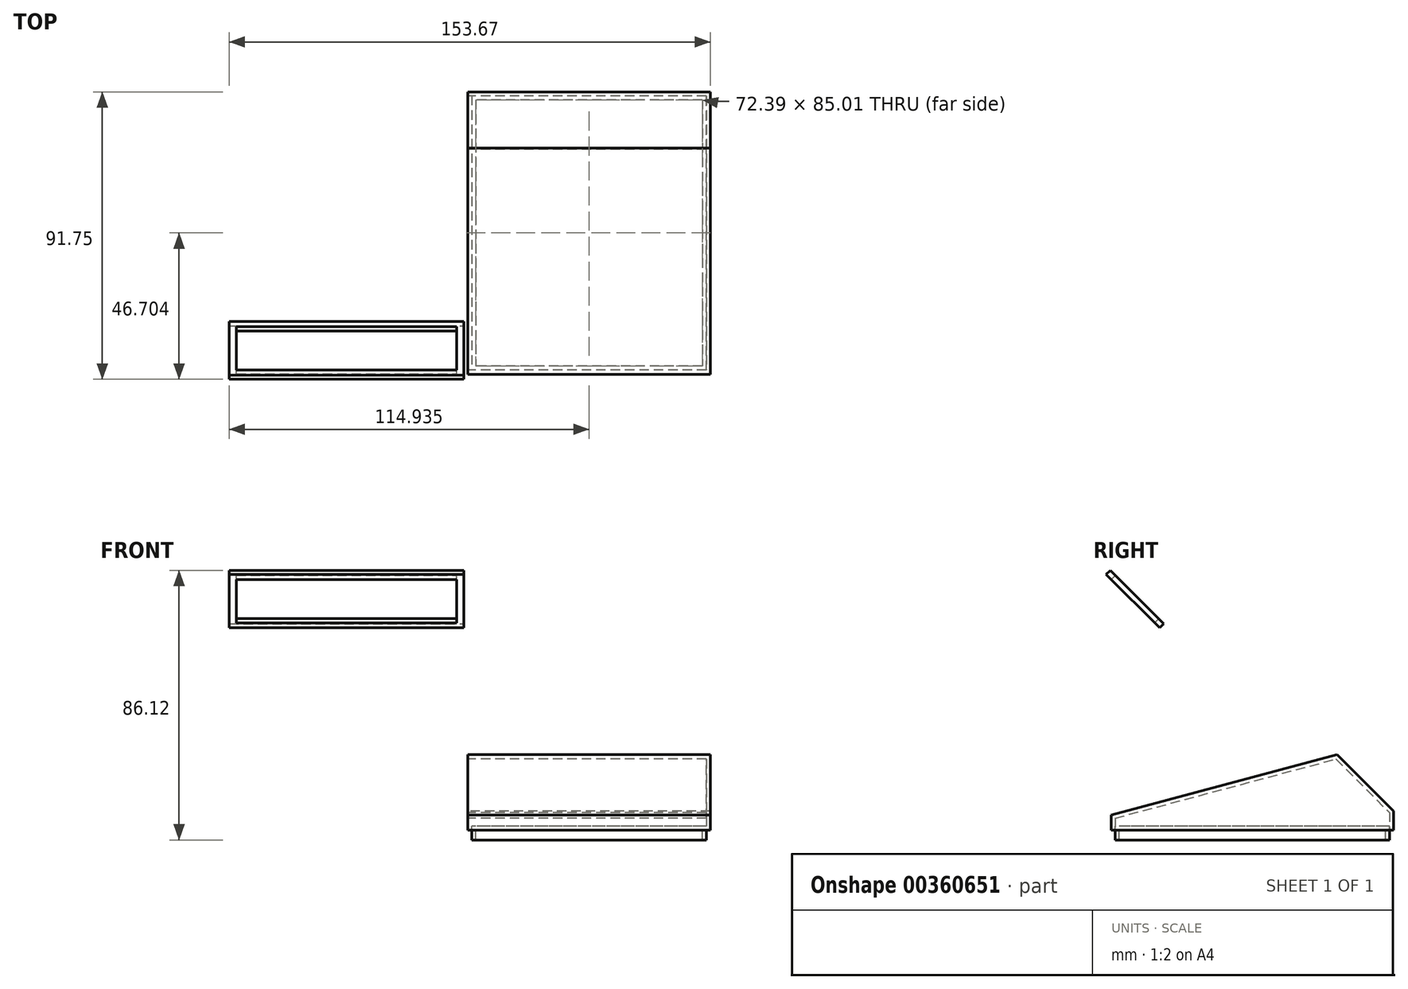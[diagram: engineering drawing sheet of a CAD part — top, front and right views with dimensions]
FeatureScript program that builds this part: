
annotation { "Feature Type Name" : "Feature", "Feature Type Description" : "" }
export const myFeature = defineFeature(function(context is Context, id is Id, definition is map)
    precondition{}
    {
        {
            var Q0;
            Q0=qCreatedBy(makeId("Right.planeOp"),FACE);
            var sketch = newSketch(context, id + "F0", { "sketchPlane" : qUnion([Q0])});
            skLineSegment(sketch, "E0", {"start": v(90.17, 0) * mm, "end": v(88.9, 0) * mm});
            skLineSegment(sketch, "E1", {"start": v(0, 4.76) * mm, "end": v(72.2, 24.05) * mm});
            skLineSegment(sketch, "E2", {"start": v(72.2, 24.05) * mm, "end": v(90.17, 6.1) * mm});
            skLineSegment(sketch, "E3", {"start": v(90.17, 6.1) * mm, "end": v(90.17, 0) * mm});
            skLineSegment(sketch, "E4.0", {"start": v(88.9, 5.57) * mm, "end": v(88.9, 0) * mm});
            skLineSegment(sketch, "E4.1", {"start": v(71.83, 22.64) * mm, "end": v(88.9, 5.57) * mm});
            skLineSegment(sketch, "E4.2", {"start": v(1.35, 3.8) * mm, "end": v(71.83, 22.64) * mm});
            skLineSegment(sketch, "E5", {"start": v(0, 4.76) * mm, "end": v(0, 0) * mm});
            skLineSegment(sketch, "E6", {"start": v(1.35, 3.8) * mm, "end": v(1.35, 0) * mm});
            skLineSegment(sketch, "E7.trimOffspring", {"start": v(1.35, 0) * mm, "end": v(0, 0) * mm});
            skLineSegment(sketch, "E8", {"start": v(88.9, 0) * mm, "end": v(90.17, 0) * mm});
            skLineSegment(sketch, "E9", {"start": v(0, 0) * mm, "end": v(1.35, 0) * mm});
            skSolve(sketch);
        }
        {
            var Q0;
            Q0 = qSketchRegion(id + "F0", true);
            extrude(context, id + "F1", {"entities" : qUnion([Q0]), "depth" : 77.47 * mm, "offsetDistance" : 25.4 * mm});
        }
        {
            var Q0;
            Q0=makeQuery(id+"F1.opExtrude","CAP_FACE",FACE,{"disambiguationData":[OSD([sQuery(id+"F0.wireOp",EDGE,"E1"),sQuery(id+"F0.wireOp",EDGE,"E2"),sQuery(id+"F0.wireOp",EDGE,"E3"),sQuery(id+"F0.wireOp",EDGE,"E4.0"),sQuery(id+"F0.wireOp",EDGE,"E4.1"),sQuery(id+"F0.wireOp",EDGE,"E4.2"),sQuery(id+"F0.wireOp",EDGE,"E5"),sQuery(id+"F0.wireOp",EDGE,"E6"),sQuery(id+"F0.wireOp",EDGE,"E8"),sQuery(id+"F0.wireOp",EDGE,"E9")])],"isStart":false});
            var sketch = newSketch(context, id + "F2", { "sketchPlane" : qUnion([Q0])});
            skLineSegment(sketch, "E10", {"start": v(90.17, 0) * mm, "end": v(0, 0) * mm});
            skLineSegment(sketch, "E11.0", {"start": v(0, 4.76) * mm, "end": v(72.2, 24.05) * mm});
            skLineSegment(sketch, "E11.1", {"start": v(0, 4.76) * mm, "end": v(0, 0) * mm});
            skLineSegment(sketch, "E11.2", {"start": v(72.2, 24.05) * mm, "end": v(90.17, 6.1) * mm});
            skLineSegment(sketch, "E11.3", {"start": v(90.17, 6.1) * mm, "end": v(90.17, 0) * mm});
            skSolve(sketch);
        }
        {
            var Q0;
            Q0 = qSketchRegion(id + "F2", true);
            extrude(context, id + "F3", {"entities" : qUnion([Q0]), "operationType" : NewBodyOperationType.ADD, "oppositeDirection" : true, "depth" : 1.27 * mm, "offsetDistance" : 25.4 * mm});
        }
        {
            var Q0;
            Q0=makeQuery(id+"F3.boolean.opBoolean","MERGE",FACE,{"derivedFrom":[makeQuery(id+"F1.opExtrude","CAP_FACE",FACE,{"disambiguationData":[OSD([sQuery(id+"F0.wireOp",EDGE,"E1"),sQuery(id+"F0.wireOp",EDGE,"E2"),sQuery(id+"F0.wireOp",EDGE,"E3"),sQuery(id+"F0.wireOp",EDGE,"E4.0"),sQuery(id+"F0.wireOp",EDGE,"E4.1"),sQuery(id+"F0.wireOp",EDGE,"E4.2"),sQuery(id+"F0.wireOp",EDGE,"E5"),sQuery(id+"F0.wireOp",EDGE,"E6"),sQuery(id+"F0.wireOp",EDGE,"E8"),sQuery(id+"F0.wireOp",EDGE,"E9")])],"isStart":false}),makeQuery(id+"F3.opExtrude","CAP_FACE",FACE,{"disambiguationData":[OSD([sQuery(id+"F2.wireOp",EDGE,"E10"),sQuery(id+"F2.wireOp",EDGE,"E11.0"),sQuery(id+"F2.wireOp",EDGE,"E11.1"),sQuery(id+"F2.wireOp",EDGE,"E11.2"),sQuery(id+"F2.wireOp",EDGE,"E11.3")])],"isStart":true})]});
            var Q1;
            Q1=makeQuery(id+"F1.opExtrude","CAP_FACE",FACE,{"disambiguationData":[OSD([sQuery(id+"F0.wireOp",EDGE,"E1"),sQuery(id+"F0.wireOp",EDGE,"E2"),sQuery(id+"F0.wireOp",EDGE,"E3"),sQuery(id+"F0.wireOp",EDGE,"E4.0"),sQuery(id+"F0.wireOp",EDGE,"E4.1"),sQuery(id+"F0.wireOp",EDGE,"E4.2"),sQuery(id+"F0.wireOp",EDGE,"E5"),sQuery(id+"F0.wireOp",EDGE,"E6"),sQuery(id+"F0.wireOp",EDGE,"E8"),sQuery(id+"F0.wireOp",EDGE,"E9")])],"isStart":true});
            cPlane(context, id + "F4", {"entities" : qUnion([Q0, Q1]), "cplaneType" : CPlaneType.MID_PLANE, "offset" : 25.4 * mm, "width" : 152.4 * mm, "height" : 152.4 * mm});
        }
        {
            var Q0;
            {var subQ0=sQuery(id+"F2.wireOp",EDGE,"E10");Q0=makeQuery(id+"FamEGNvEXDgyTqM_1.1.F3.boolean.opBoolean","MERGE",FACE,{"derivedFrom":[makeQuery(id+"F3.boolean.opBoolean","MERGE",FACE,{"derivedFrom":[makeQuery(id+"F1.opExtrude","SWEPT_FACE",FACE,{"disambiguationData":[OSD([sQuery(id+"F0.wireOp",EDGE,"E8")])]}),makeQuery(id+"F1.opExtrude","SWEPT_FACE",FACE,{"disambiguationData":[OSD([sQuery(id+"F0.wireOp",EDGE,"E9")])]}),makeQuery(id+"F3.opExtrude","SWEPT_FACE",FACE,{"disambiguationData":[OSD([subQ0])]})]}),makeQuery(id+"FamEGNvEXDgyTqM_1.1.F3.opExtrude","SWEPT_FACE",FACE,{"disambiguationData":[OSD([subQ0])]})]});}
            var sketch = newSketch(context, id + "F5", { "sketchPlane" : qUnion([Q0])});
            skLineSegment(sketch, "E12.0", {"start": v(76.2, -1.35) * mm, "end": v(1.27, -1.35) * mm});
            skLineSegment(sketch, "E12.1", {"start": v(1.27, -88.9) * mm, "end": v(1.27, -1.35) * mm});
            skLineSegment(sketch, "E12.2", {"start": v(76.2, -88.9) * mm, "end": v(76.2, -1.35) * mm});
            skLineSegment(sketch, "E12.3", {"start": v(76.2, -88.9) * mm, "end": v(1.27, -88.9) * mm});
            skLineSegment(sketch, "E13.0", {"start": v(74.93, -2.62) * mm, "end": v(2.54, -2.62) * mm});
            skLineSegment(sketch, "E13.1", {"start": v(74.93, -87.63) * mm, "end": v(74.93, -2.62) * mm});
            skLineSegment(sketch, "E13.2", {"start": v(74.93, -87.63) * mm, "end": v(2.54, -87.63) * mm});
            skLineSegment(sketch, "E13.3", {"start": v(2.54, -87.63) * mm, "end": v(2.54, -2.62) * mm});
            skSolve(sketch);
        }
        {
            var Q0;
            Q0 = qSketchRegion(id + "F5", true);
            extrude(context, id + "F6", {"entities" : qUnion([Q0]), "operationType" : NewBodyOperationType.ADD, "depth" : 3.17 * mm, "offsetDistance" : 25.4 * mm, "hasSecondDirection" : true, "secondDirectionOppositeDirection" : true, "secondDirectionDepth" : 1.27 * mm});
        }
        {
            var Q0;
            Q0=makeQuery(id+"F1.opExtrude","SWEPT_FACE",FACE,{"disambiguationData":[OSD([sQuery(id+"F0.wireOp",EDGE,"E2")])]});
            var sketch = newSketch(context, id + "F7", { "sketchPlane" : qUnion([Q0])});
            skLineSegment(sketch, "E14", {"start": v(77.47, 46.75) * mm, "end": v(0, 46.75) * mm, "construction": true});
            skLineSegment(sketch, "E15", {"start": v(38.73, 34.05) * mm, "end": v(38.74, 59.45) * mm, "construction": true});
            skLineSegment(sketch, "E16.bottom", {"start": v(76.2, 34.69) * mm, "end": v(1.27, 34.69) * mm});
            skLineSegment(sketch, "E16.top", {"start": v(76.2, 58.82) * mm, "end": v(1.27, 58.82) * mm});
            skLineSegment(sketch, "E16.left", {"start": v(76.2, 34.69) * mm, "end": v(76.2, 58.82) * mm});
            skLineSegment(sketch, "E16.right", {"start": v(1.27, 34.69) * mm, "end": v(1.27, 58.82) * mm});
            skPoint(sketch, "E16.middle", {"position": v(38.73, 46.75) * mm});
            skSolve(sketch);
        }
        {
            var Q0;
            Q0 = qSketchRegion(id + "F7", true);
            extrude(context, id + "F8", {"entities" : qUnion([Q0]), "operationType" : NewBodyOperationType.REMOVE, "oppositeDirection" : true, "depth" : 9.58 * mm, "offsetDistance" : 25.4 * mm});
        }
        {
            var Q0;
            Q0=makeQuery(id+"F1.opExtrude","SWEPT_FACE",FACE,{"disambiguationData":[OSD([sQuery(id+"F0.wireOp",EDGE,"E2")])]});
            cPlane(context, id + "F9", {"entities" : qUnion([Q0]), "cplaneType" : CPlaneType.OFFSET, "offset" : 9.58 * mm, "oppositeDirection" : true, "width" : 152.4 * mm, "height" : 152.4 * mm});
        }
        {
            var Q0;
            Q0=qCreatedBy(id+"F9.planeOp",FACE);
            var sketch = newSketch(context, id + "F10", { "sketchPlane" : qUnion([Q0])});
            skLineSegment(sketch, "E17.0", {"start": v(76.2, 34.69) * mm, "end": v(1.27, 34.69) * mm});
            skLineSegment(sketch, "E17.1", {"start": v(76.2, 34.69) * mm, "end": v(76.2, 58.82) * mm});
            skLineSegment(sketch, "E17.2", {"start": v(76.2, 58.82) * mm, "end": v(1.27, 58.82) * mm});
            skLineSegment(sketch, "E17.3", {"start": v(1.27, 34.69) * mm, "end": v(1.27, 58.82) * mm});
            skLineSegment(sketch, "E18.0", {"start": v(73.91, 36.97) * mm, "end": v(73.91, 56.53) * mm});
            skLineSegment(sketch, "E18.1", {"start": v(73.91, 36.97) * mm, "end": v(3.56, 36.97) * mm});
            skLineSegment(sketch, "E18.2", {"start": v(3.56, 36.97) * mm, "end": v(3.56, 56.53) * mm});
            skLineSegment(sketch, "E18.3", {"start": v(73.91, 56.53) * mm, "end": v(3.56, 56.53) * mm});
            skSolve(sketch);
        }
        {
            var Q0;
            Q0 = qSketchRegion(id + "F10", true);
            extrude(context, id + "F11", {"entities" : qUnion([Q0]), "operationType" : NewBodyOperationType.ADD, "oppositeDirection" : true, "depth" : 1.9 * mm, "offsetDistance" : 25.4 * mm});
        }
    });
